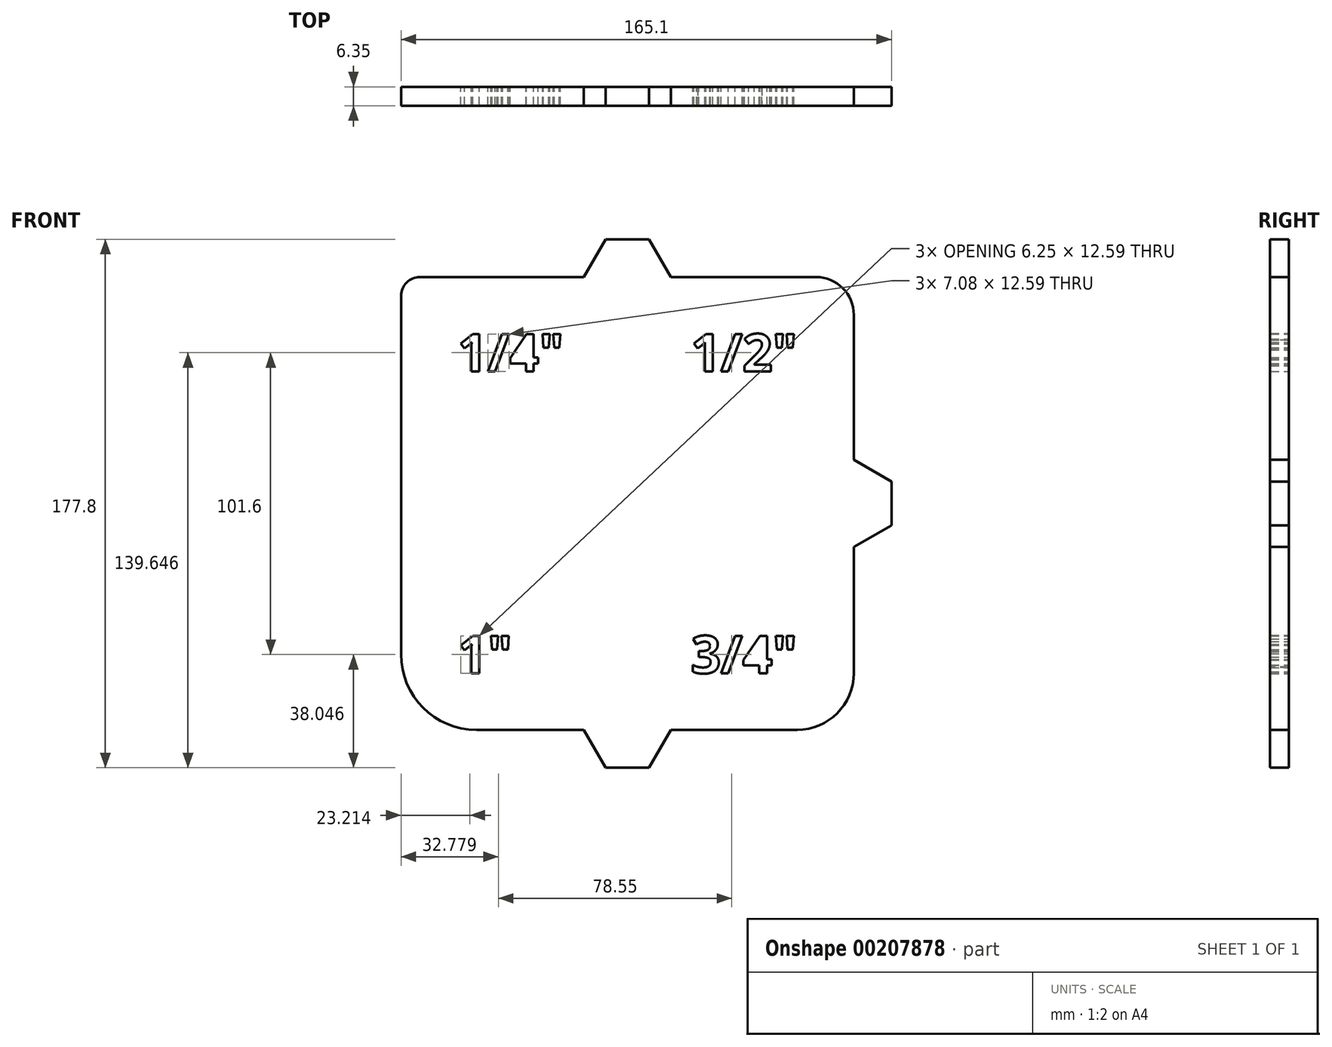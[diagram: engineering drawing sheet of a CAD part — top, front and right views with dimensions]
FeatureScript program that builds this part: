
annotation { "Feature Type Name" : "Feature", "Feature Type Description" : "" }
export const myFeature = defineFeature(function(context is Context, id is Id, definition is map)
    precondition{}
    {
        {
            var Q0;
            Q0=qCreatedBy(makeId("Front.planeOp"),FACE);
            var sketch = newSketch(context, id + "F0", { "sketchPlane" : qUnion([Q0])});
            skLineSegment(sketch, "E0.bottom", {"start": v(-69.85, 76.2) * mm, "end": v(63.5, 76.2) * mm});
            skLineSegment(sketch, "E0.top", {"start": v(-50.8, -76.2) * mm, "end": v(57.15, -76.2) * mm});
            skLineSegment(sketch, "E0.left", {"start": v(-76.2, 69.85) * mm, "end": v(-76.2, 14.66) * mm});
            skLineSegment(sketch, "E0.right", {"start": v(76.2, 63.5) * mm, "end": v(76.2, -57.15) * mm});
            skPoint(sketch, "E0.middle", {"position": v(0, 0) * mm});
            skPoint(sketch, "E1.visualSharp", {"position": v(-76.2, 76.2) * mm});
            skArc(sketch, "E1.filletArc", {"start": v(-69.85, 76.2) * mm, "mid": v(-74.34, 74.34) * mm, "end": v(-76.2, 69.85) * mm});
            skPoint(sketch, "E2.visualSharp", {"position": v(76.2, 76.2) * mm});
            skArc(sketch, "E2.filletArc", {"start": v(76.2, 63.5) * mm, "mid": v(72.48, 72.48) * mm, "end": v(63.5, 76.2) * mm});
            skPoint(sketch, "E3.visualSharp", {"position": v(76.2, -76.2) * mm});
            skArc(sketch, "E3.filletArc", {"start": v(57.15, -76.2) * mm, "mid": v(70.62, -70.62) * mm, "end": v(76.2, -57.15) * mm});
            skPoint(sketch, "E4.visualSharp", {"position": v(-76.2, -76.2) * mm});
            skArc(sketch, "E4.filletArc", {"start": v(-76.2, -50.8) * mm, "mid": v(-68.76, -68.76) * mm, "end": v(-50.8, -76.2) * mm});
            skLineSegment(sketch, "E5.trimOffspring", {"start": v(-76.2, -14.66) * mm, "end": v(-76.2, -50.8) * mm});
            skLineSegment(sketch, "E6", {"start": v(-76.2, 76.2) * mm, "end": v(76.2, -76.2) * mm, "construction": true});
            skLineSegment(sketch, "E7", {"start": v(-76.2, -76.2) * mm, "end": v(76.2, 76.2) * mm, "construction": true});
            skText(sketch, "E8", { "text": "1/4\"", "fontName": "OpenSans-Bold.ttf"});
            skText(sketch, "E9", { "text": "1/2\"", "fontName": "OpenSans-Bold.ttf"});
            skText(sketch, "E10", { "text": "1\"", "fontName": "OpenSans-Bold.ttf"});
            skText(sketch, "E11", { "text": "3/4\"", "fontName": "OpenSans-Bold.ttf"});
            skLineSegment(sketch, "E12.0", {"start": v(76.2, 14.66) * mm, "end": v(88.9, 7.33) * mm});
            skLineSegment(sketch, "E12.1", {"start": v(88.9, 7.33) * mm, "end": v(88.9, -7.33) * mm});
            skLineSegment(sketch, "E12.2", {"start": v(88.9, -7.33) * mm, "end": v(76.2, -14.66) * mm});
            skLineSegment(sketch, "E13.3", {"start": v(-14.66, 76.2) * mm, "end": v(-7.33, 88.9) * mm});
            skLineSegment(sketch, "E13.4", {"start": v(-7.33, 88.9) * mm, "end": v(7.33, 88.9) * mm});
            skLineSegment(sketch, "E13.5", {"start": v(7.33, 88.9) * mm, "end": v(14.66, 76.2) * mm});
            skLineSegment(sketch, "E14.0", {"start": v(14.66, -76.2) * mm, "end": v(7.33, -88.9) * mm});
            skLineSegment(sketch, "E14.1", {"start": v(7.33, -88.9) * mm, "end": v(-7.33, -88.9) * mm});
            skLineSegment(sketch, "E14.2", {"start": v(-7.33, -88.9) * mm, "end": v(-14.66, -76.2) * mm});
            skLineSegment(sketch, "E15", {"start": v(-76.2, 14.66) * mm, "end": v(-76.2, -14.66) * mm});
            skLineSegment(sketch, "E16", {"start": v(-76.2, 0) * mm, "end": v(-82.55, 0) * mm});
            skLineSegment(sketch, "E17", {"start": v(-79.38, 0) * mm, "end": v(-79.38, 4.44) * mm, "construction": true});
            skPoint(sketch, "E17.endSnap0", {"position": v(-79.38, 0) * mm});
            skLineSegment(sketch, "E18.MirrorCS", {"start": v(-79.38, 0) * mm, "end": v(-79.37, -4.45) * mm, "construction": true});
            skArc(sketch, "E19.0.endCap", {"start": v(-82.55, 4.44) * mm, "mid": v(-79.37, 7.62) * mm, "end": v(-76.2, 4.44) * mm});
            skLineSegment(sketch, "E19.0.left", {"start": v(-82.55, -1.9) * mm, "end": v(-82.55, 4.44) * mm});
            skLineSegment(sketch, "E19.0.right", {"start": v(-76.2, -1.9) * mm, "end": v(-76.2, 4.44) * mm});
            skArc(sketch, "E19.1.endCap", {"start": v(-76.2, -4.45) * mm, "mid": v(-79.37, -7.62) * mm, "end": v(-82.55, -4.45) * mm});
            skLineSegment(sketch, "E19.1.left", {"start": v(-76.2, 1.9) * mm, "end": v(-76.2, -4.45) * mm});
            skLineSegment(sketch, "E19.1.right", {"start": v(-82.55, 1.9) * mm, "end": v(-82.55, -4.45) * mm});
            skLineSegment(sketch, "E20", {"start": v(-76.2, -14.66) * mm, "end": v(-83.04, -9.84) * mm});
            skLineSegment(sketch, "E21", {"start": v(-85.73, -4.65) * mm, "end": v(-85.73, 4.98) * mm});
            skLineSegment(sketch, "E22", {"start": v(-82.86, 10.28) * mm, "end": v(-76.2, 14.66) * mm});
            skPoint(sketch, "E23.visualSharp", {"position": v(-85.73, -7.94) * mm});
            skArc(sketch, "E23.filletArc", {"start": v(-85.73, -4.65) * mm, "mid": v(-85.01, -7.57) * mm, "end": v(-83.04, -9.84) * mm});
            skPoint(sketch, "E24.visualSharp", {"position": v(-85.73, 8.4) * mm});
            skArc(sketch, "E24.filletArc", {"start": v(-82.86, 10.28) * mm, "mid": v(-84.96, 8) * mm, "end": v(-85.73, 4.98) * mm});
            skLineSegment(sketch, "E25", {"start": v(-226.65, 33.46) * mm, "end": v(-226.65, 4.13) * mm});
            skLineSegment(sketch, "E26", {"start": v(-226.65, 18.8) * mm, "end": v(-233, 18.8) * mm});
            skLineSegment(sketch, "E27", {"start": v(-229.82, 18.8) * mm, "end": v(-229.82, 23.24) * mm, "construction": true});
            skPoint(sketch, "E27.endSnap0", {"position": v(-229.82, 18.8) * mm});
            skLineSegment(sketch, "E28.MirrorCS", {"start": v(-229.82, 18.8) * mm, "end": v(-229.82, 14.35) * mm, "construction": true});
            skArc(sketch, "E29.0.endCap", {"start": v(-233, 23.24) * mm, "mid": v(-229.82, 26.41) * mm, "end": v(-226.65, 23.24) * mm});
            skLineSegment(sketch, "E29.0.left", {"start": v(-233, 16.89) * mm, "end": v(-233, 23.24) * mm});
            skLineSegment(sketch, "E29.0.right", {"start": v(-226.65, 16.89) * mm, "end": v(-226.65, 23.24) * mm});
            skArc(sketch, "E29.1.endCap", {"start": v(-226.65, 14.35) * mm, "mid": v(-229.82, 11.17) * mm, "end": v(-233, 14.35) * mm});
            skLineSegment(sketch, "E29.1.left", {"start": v(-226.65, 20.7) * mm, "end": v(-226.65, 14.35) * mm});
            skLineSegment(sketch, "E29.1.right", {"start": v(-233, 20.7) * mm, "end": v(-233, 14.35) * mm});
            skLineSegment(sketch, "E30", {"start": v(-226.65, 4.13) * mm, "end": v(-233.49, 8.95) * mm});
            skLineSegment(sketch, "E31", {"start": v(-236.17, 14.14) * mm, "end": v(-236.17, 23.77) * mm});
            skLineSegment(sketch, "E32", {"start": v(-233.31, 29.08) * mm, "end": v(-226.65, 33.46) * mm});
            skPoint(sketch, "E33.visualSharp", {"position": v(-236.17, 10.85) * mm});
            skArc(sketch, "E33.filletArc", {"start": v(-236.17, 14.14) * mm, "mid": v(-235.46, 11.22) * mm, "end": v(-233.49, 8.95) * mm});
            skPoint(sketch, "E34.visualSharp", {"position": v(-236.17, 27.2) * mm});
            skArc(sketch, "E34.filletArc", {"start": v(-233.31, 29.08) * mm, "mid": v(-235.41, 26.78) * mm, "end": v(-236.17, 23.77) * mm});
            const initialGuessF0  = {"E8": [-0.05715, 0.04445, 1, 0, 0.0127], "E9": [0.0214, 0.04445, 1, 0, 0.0127], "E10": [-0.05715, -0.05715, 1, 0, 0.0127], "E11": [0.0214, -0.05715, 1, 0, 0.0127]};
            skSetInitialGuess(sketch, initialGuessF0);
            skSolve(sketch);
        }
        {
            var Q0;
            {var subQ5=sQuery(id+"F0.wireOp",EDGE,"ba177b99-28a8-4f5b-bfe7-87b83c7c003b.5");Q0=makeQuery(id+"F0.imprint","IMPRINT",FACE,{"disambiguationData":[TD([[makeQuery(id+"F0.imprint","IMPRINT",EDGE,{"derivedFrom":subQ5}),-1.0]])]});}
            var Q1;
            {var subQ7=sQuery(id+"F0.wireOp",EDGE,"ba177b99-28a8-4f5b-bfe7-87b83c7c003b.3");Q1=makeQuery(id+"F0.imprint","IMPRINT",FACE,{"disambiguationData":[TD([[makeQuery(id+"F0.imprint","IMPRINT",EDGE,{"derivedFrom":subQ7}),-1.0]])]});}
            var Q2;
            {var subQ14=sQuery(id+"F0.wireOp",EDGE,"E0.left");Q2=makeQuery(id+"F0.imprint","IMPRINT",FACE,{"disambiguationData":[TD([[makeQuery(id+"F0.imprint","IMPRINT",EDGE,{"derivedFrom":subQ14}),1.0]])]});}
            var Q3;
            {var subQ0=sQuery(id+"F0.wireOp",EDGE,"E13.3");Q3=makeQuery(id+"F0.imprint","IMPRINT",FACE,{"disambiguationData":[TD([[makeQuery(id+"F0.imprint","IMPRINT",EDGE,{"derivedFrom":subQ0}),-1.0]])]});}
            var Q4;
            {var subQ0=sQuery(id+"F0.wireOp",EDGE,"E12.0");Q4=makeQuery(id+"F0.imprint","IMPRINT",FACE,{"disambiguationData":[TD([[makeQuery(id+"F0.imprint","IMPRINT",EDGE,{"derivedFrom":subQ0}),-1.0]])]});}
            var Q5;
            {var subQ0=sQuery(id+"F0.wireOp",EDGE,"E14.0");Q5=makeQuery(id+"F0.imprint","IMPRINT",FACE,{"disambiguationData":[TD([[makeQuery(id+"F0.imprint","IMPRINT",EDGE,{"derivedFrom":subQ0}),-1.0]])]});}
            extrude(context, id + "F1", {"entities" : qUnion([Q0, Q1, Q2, Q3, Q4, Q5]), "depth" : 6.35 * mm});
        }
    });
